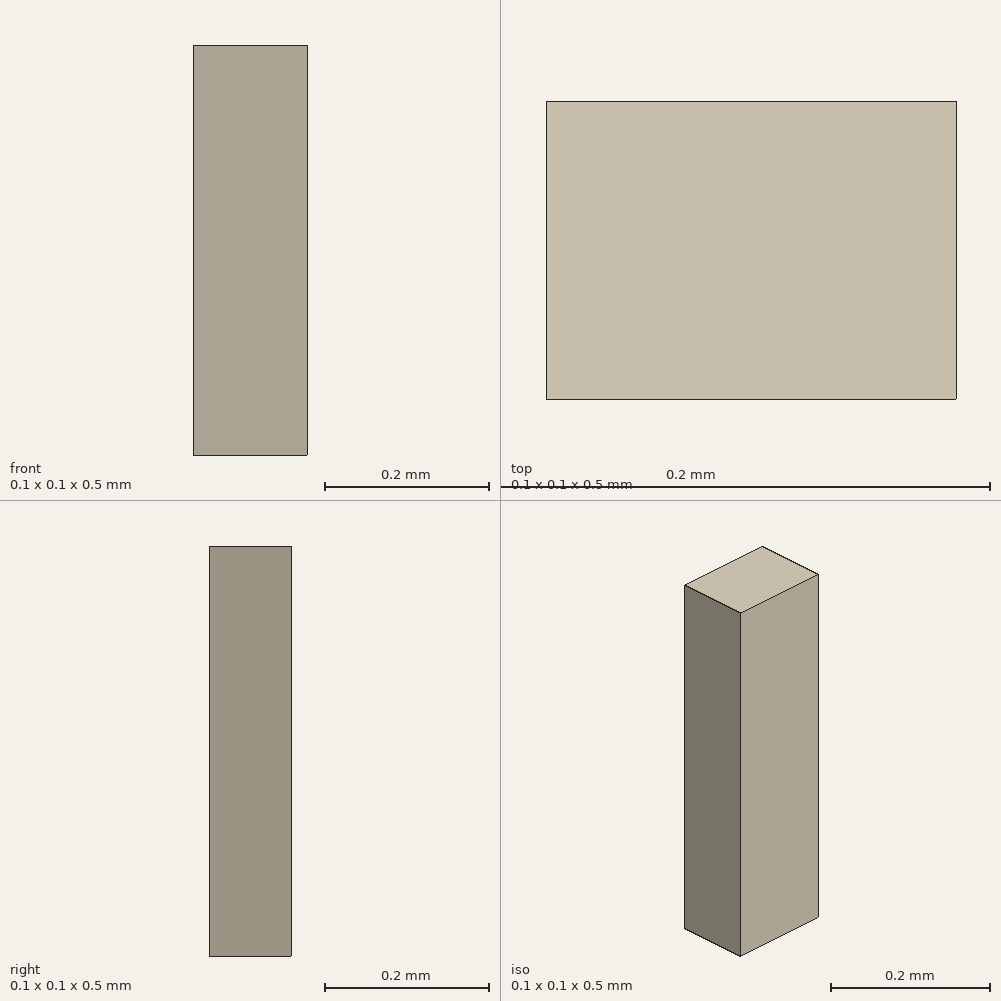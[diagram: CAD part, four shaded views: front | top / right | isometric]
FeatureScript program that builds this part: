
annotation { "Feature Type Name" : "Feature", "Feature Type Description" : "" }
export const myFeature = defineFeature(function(context is Context, id is Id, definition is map)
    precondition{}
    {
        {
            var Q0;
            Q0=qCreatedBy(makeId("Top.planeOp"),FACE);
            var sketch = newSketch(context, id + "F0", { "sketchPlane" : qUnion([Q0])});
            skLineSegment(sketch, "E0.bottom", {"start": v(0, 0) * mm, "end": v(0.14, 0) * mm});
            skLineSegment(sketch, "E0.top", {"start": v(0, 0.1) * mm, "end": v(0.14, 0.1) * mm});
            skLineSegment(sketch, "E0.left", {"start": v(0, 0) * mm, "end": v(0, 0.1) * mm});
            skLineSegment(sketch, "E0.right", {"start": v(0.14, 0) * mm, "end": v(0.14, 0.1) * mm});
            skSolve(sketch);
        }
        {
            var Q0;
            Q0=makeQuery(id+"F0.imprint","IMPRINT",FACE,{"disambiguationData":[TD([[makeQuery(id+"F0.imprint","IMPRINT",EDGE,{"derivedFrom":sQuery(id+"F0.wireOp",EDGE,"E0.bottom")}),1.0]])]});
            extrude(context, id + "F1", {"entities" : qUnion([Q0]), "depth" : .5 * mm, "offsetDistance" : 25 * mm});
        }
    });
